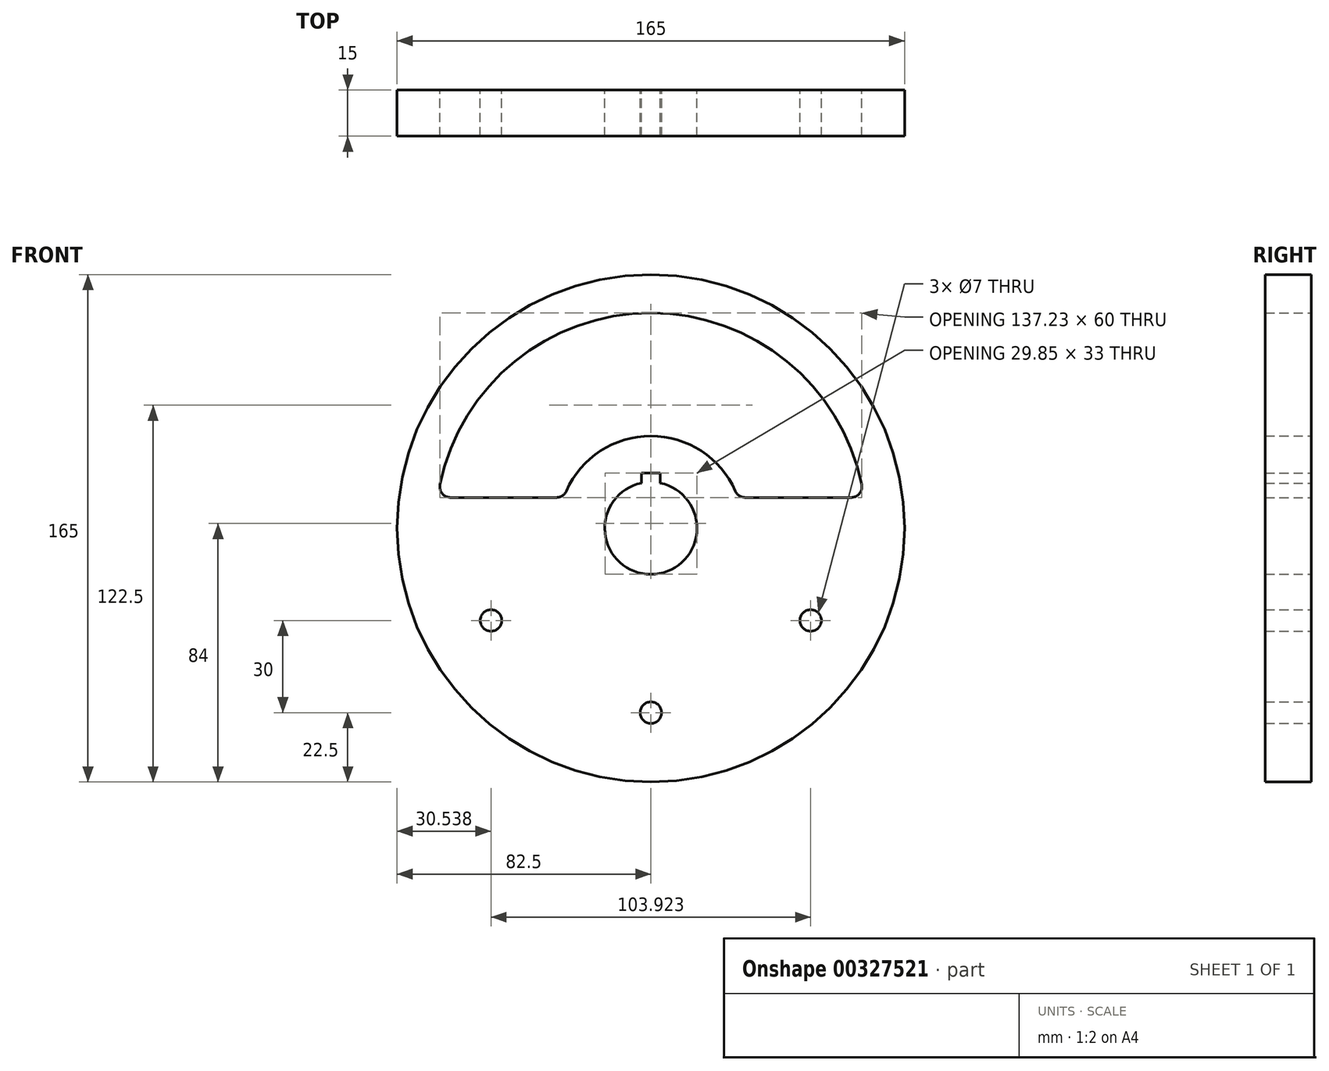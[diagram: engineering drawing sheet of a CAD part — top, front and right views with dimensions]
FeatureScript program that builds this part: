
annotation { "Feature Type Name" : "Feature", "Feature Type Description" : "" }
export const myFeature = defineFeature(function(context is Context, id is Id, definition is map)
    precondition{}
    {
        {
            var Q0;
            Q0=qCreatedBy(makeId("Front.planeOp"),FACE);
            var sketch = newSketch(context, id + "F0", { "sketchPlane" : qUnion([Q0])});
            skCircle(sketch, "E0", {"center": v(0, 0) * mm, "radius": 82.5 * mm});
            skLineSegment(sketch, "E1.trimOffspring", {"start": v(0, -55) * mm, "end": v(0, -60) * mm});
            skLineSegment(sketch, "E2", {"start": v(0, 0) * mm, "end": v(0, -12.5) * mm});
            skArc(sketch, "E3", {"start": v(-3, 14.7) * mm, "mid": v(0, -15) * mm, "end": v(3, 14.7) * mm});
            skLineSegment(sketch, "E4", {"start": v(0, 0) * mm, "end": v(0, 15) * mm});
            skLineSegment(sketch, "E5", {"start": v(0, 15) * mm, "end": v(0, 18) * mm});
            skLineSegment(sketch, "E6", {"start": v(0, 18) * mm, "end": v(3, 18) * mm});
            skLineSegment(sketch, "E7", {"start": v(3, 18) * mm, "end": v(3, 14.7) * mm});
            skLineSegment(sketch, "E8.MirrorCS", {"start": v(0, 18) * mm, "end": v(-3, 18) * mm});
            skLineSegment(sketch, "E9.MirrorCS", {"start": v(-3, 18) * mm, "end": v(-3, 14.7) * mm});
            skLineSegment(sketch, "E10", {"start": v(0, 82.5) * mm, "end": v(0, -82.5) * mm, "construction": true});
            skLineSegment(sketch, "E11", {"start": v(82.5, 0) * mm, "end": v(-82.5, 0) * mm, "construction": true});
            skLineSegment(sketch, "E12", {"start": v(-69.28, 10) * mm, "end": v(-28.28, 10) * mm});
            skArc(sketch, "E13", {"start": v(-69.28, 10) * mm, "mid": v(0, -70) * mm, "end": v(69.28, 10) * mm, "construction": true});
            skArc(sketch, "E14", {"start": v(69.28, 10) * mm, "mid": v(0, 70) * mm, "end": v(-69.28, 10) * mm});
            skArc(sketch, "E15", {"start": v(-28.28, 10) * mm, "mid": v(0, -30) * mm, "end": v(28.28, 10) * mm, "construction": true});
            skArc(sketch, "E16", {"start": v(28.28, 10) * mm, "mid": v(0, 30) * mm, "end": v(-28.28, 10) * mm});
            skLineSegment(sketch, "E17.trimOffspring", {"start": v(28.28, 10) * mm, "end": v(69.28, 10) * mm});
            skLineSegment(sketch, "E18", {"start": v(0, 0) * mm, "end": v(51.96, -30) * mm});
            skCircle(sketch, "E19", {"center": v(51.96, -30) * mm, "radius": 3.5 * mm});
            skCircle(sketch, "E20.MirrorC", {"center": v(-51.96, -30) * mm, "radius": 3.5 * mm});
            skCircle(sketch, "E21", {"center": v(0, -60) * mm, "radius": 3.5 * mm});
            skSolve(sketch);
        }
        {
            var Q0;
            Q0=makeQuery(id+"F0.imprint","IMPRINT",FACE,{"disambiguationData":[TD([[makeQuery(id+"F0.imprint","IMPRINT",EDGE,{"derivedFrom":sQuery(id+"F0.wireOp",EDGE,"E0")}),1.0]])]});
            extrude(context, id + "F1", {"entities" : qUnion([Q0]), "depth" : 15 * mm});
        }
        {
            var Q0;
            Q0=makeQuery(id+"F1.opExtrude","SWEPT_EDGE",EDGE,{"disambiguationData":[OSD([sQuery(id+"F0.wireOp",EDGE,"E14"),sQuery(id+"F0.wireOp",EDGE,"E17.trimOffspring")])]});
            var Q1;
            Q1=makeQuery(id+"F1.opExtrude","SWEPT_EDGE",EDGE,{"disambiguationData":[OSD([sQuery(id+"F0.wireOp",EDGE,"E12"),sQuery(id+"F0.wireOp",EDGE,"E14")])]});
            var Q2;
            Q2=makeQuery(id+"F1.opExtrude","SWEPT_EDGE",EDGE,{"disambiguationData":[OSD([sQuery(id+"F0.wireOp",EDGE,"E12"),sQuery(id+"F0.wireOp",EDGE,"E16")])]});
            var Q3;
            Q3=makeQuery(id+"F1.opExtrude","SWEPT_EDGE",EDGE,{"disambiguationData":[OSD([sQuery(id+"F0.wireOp",EDGE,"E16"),sQuery(id+"F0.wireOp",EDGE,"E17.trimOffspring")])]});
            fillet(context, id + "F2", {"entities" : qUnion([Q0, Q1, Q2, Q3]), "radius" : 3.5 * mm, "tangentPropagation" : true, "allowEdgeOverflow" : false});
        }
    });
